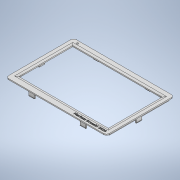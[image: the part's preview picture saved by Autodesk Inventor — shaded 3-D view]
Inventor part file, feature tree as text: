
AUTODESK INVENTOR PART (.ipt)
format: ipt  version: 2021 (Build 250183000, 183)  size: 700,416 bytes
history: native  units: mm
features: chamfer x10, extrude x9, sketch x9, mirror x3, fillet x1
ambient origin geometry x8: Origin, YZ Plane, XZ Plane, XY Plane, X Axis, Y Axis, Z Axis, Center Point
bodies: Body1 (feature_tree)
feature tree (32):
  extrude  "Extrusion2"  Depth=124.0mm
  sketch  "Sketch2"  dims[d23=2.0mm]
  chamfer  "Chamfer6"  Distance=3.0mm
  chamfer  "Chamfer7"  Distance=4.0mm Angle=45.0deg
  chamfer  "Chamfer8"  Distance=4.0mm Angle=45.0deg
  chamfer  "Chamfer9"  Distance=4.0mm Angle=45.0deg
  extrude  "Extrusion5"  Depth=1.0mm TaperAngle=0.0deg
  fillet  "Fillet1"  Radius=13.5mm
  extrude  "Extrusion7"  Depth=2.0mm
  chamfer  "Chamfer10"  Distance=8.0mm
  chamfer  "Chamfer11"  Distance=2.0mm Angle=45.0deg
  extrude  "Extrusion8"  Depth=2.0mm
  chamfer  "Chamfer12"  Distance=0.8mm
  mirror  "Mirror1"
  mirror  "Mirror2"
  extrude  "Extrusion9"  Depth=2.0mm TaperAngle=45.0deg
  chamfer  "Chamfer13"  Distance=2.0mm
  chamfer  "Chamfer14"  Distance=10.0mm
  extrude  "Extrusion10"  Depth=8.0mm TaperAngle=0.0deg
  chamfer  "Chamfer15"  Distance=2.0mm Angle=45.0deg
  extrude  "Extrusion11"  Depth=2.0mm TaperAngle=45.0deg
  extrude  "Extrusion13"  Depth=2.0mm
  mirror  "Mirror5"
  extrude  "Extrusion14"  Depth=2.0mm TaperAngle=0.0deg
  sketch  "Sketch1"  dims[d2=184.4mm d3=124.0mm d4=3.0mm d5=0.0mm]
  sketch  "Sketch4"  dims[d26=5.0mm]
  sketch  "Sketch5"  dims[d34=164.4mm]
  sketch  "Sketch6"  dims[d35=99.0mm d36=4.0mm d37=1.0mm d38=45.0deg d39=4.0mm d40=1.0mm d41=45.0deg d42=4.0mm d43=1.0mm d44=45.0deg]
  sketch  "Sketch7"  dims[d45=4.0mm d46=1.0mm d47=45.0deg d48=1.0mm d49=0.0mm d50=13.5mm]
  sketch  "Sketch8"  dims[d53=10.0mm d54=2.0mm]
  sketch  "Sketch10"  dims[d55=40.0mm d56=8.0mm d57=0.0mm d58=2.0mm d59=2.0mm d60=45.0deg]
  sketch  "Sketch11"  dims[d61=1.0mm d62=2.0mm d63=45.0deg d64=1.0mm d65=0.8mm d66=0.0mm d67=1.0mm d68=0.8mm d69=45.0deg d70=2.0mm d72=10.0mm d73=8.0mm d74=0.0mm d75=2.0mm d76=2.0mm d77=45.0deg d78=1.0mm d79=2.0mm d80=45.0deg d81=1.0mm d82=0.8mm d83=0.0mm d84=1.0mm d85=0.8mm d86=45.0deg d87=3.2mm d88=0.0mm d89=0.0mm d93=0.4mm d94=0.0mm d95=5.0mm d96=12.2mm d97=2.0mm d98=2.0mm d99=2.0mm d100=0.0mm d101=2.0mm d0=0.5mm d1=0.872665mm d21=0.5mm d22=0.872665mm d24=0.872665mm]
